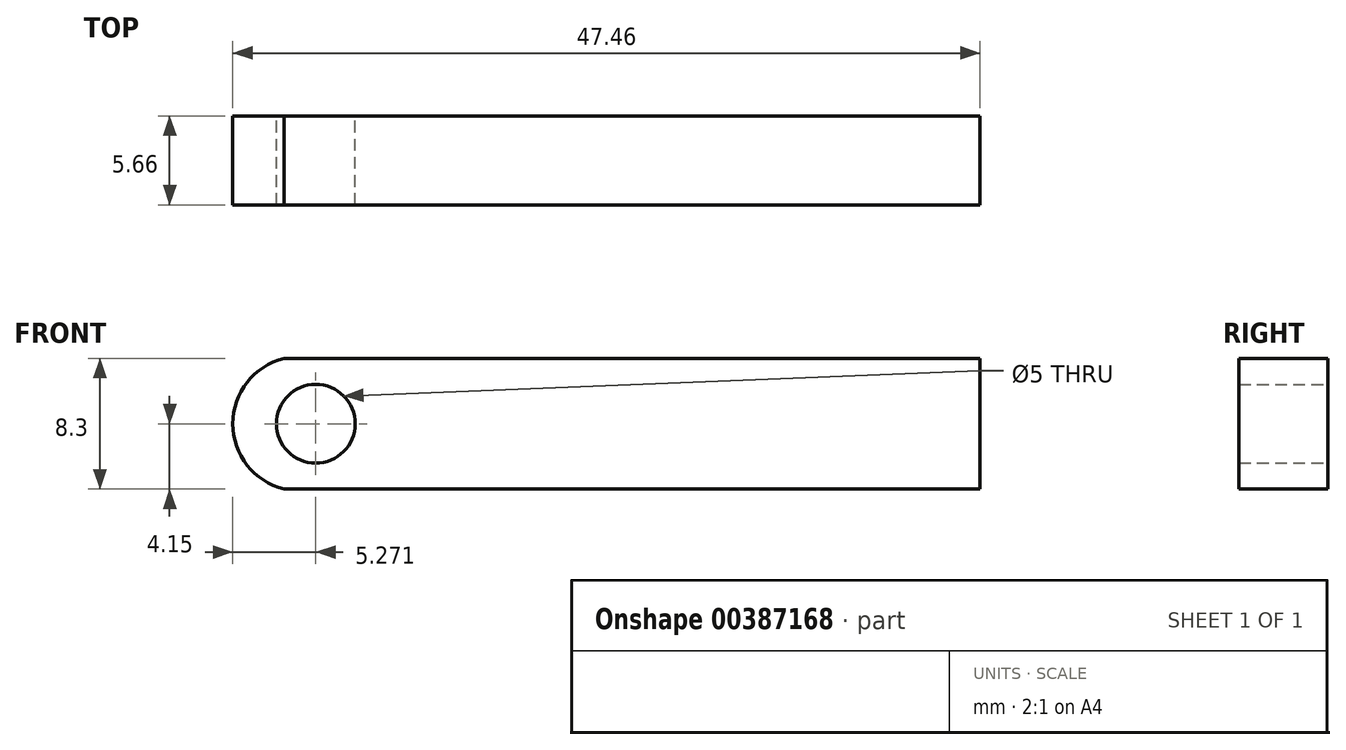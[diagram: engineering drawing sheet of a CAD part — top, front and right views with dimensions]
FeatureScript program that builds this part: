
annotation { "Feature Type Name" : "Feature", "Feature Type Description" : "" }
export const myFeature = defineFeature(function(context is Context, id is Id, definition is map)
    precondition{}
    {
        {
            var Q0;
            Q0=qCreatedBy(makeId("Front.planeOp"),FACE);
            var sketch = newSketch(context, id + "F0", { "sketchPlane" : qUnion([Q0])});
            skLineSegment(sketch, "E0", {"start": v(0, 0) * mm, "end": v(47.46, 0) * mm});
            skLineSegment(sketch, "E1", {"start": v(0, 0) * mm, "end": v(-47.46, 0) * mm});
            skLineSegment(sketch, "E2", {"start": v(0, 0) * mm, "end": v(0, 5.66) * mm});
            skLineSegment(sketch, "E3", {"start": v(0, 0) * mm, "end": v(0, -5.66) * mm});
            skLineSegment(sketch, "E4", {"start": v(47.46, 0) * mm, "end": v(44.7, 0) * mm});
            skCircle(sketch, "E5", {"center": v(42.19, 0) * mm, "radius": 2.5 * mm});
            skLineSegment(sketch, "E6", {"start": v(47.46, 0) * mm, "end": v(47.46, 4.15) * mm});
            skLineSegment(sketch, "E7", {"start": v(47.46, 4.15) * mm, "end": v(0, 4.15) * mm});
            skLineSegment(sketch, "E8.MirrorCS", {"start": v(47.46, -4.15) * mm, "end": v(0, -4.15) * mm});
            skLineSegment(sketch, "E9.MirrorCS", {"start": v(47.46, 0) * mm, "end": v(47.46, -4.15) * mm});
            skLineSegment(sketch, "E10.MirrorCS", {"start": v(-47.46, -4.15) * mm, "end": v(0, -4.15) * mm});
            skLineSegment(sketch, "E11.MirrorCS", {"start": v(-47.46, 4.15) * mm, "end": v(0, 4.15) * mm});
            skCircle(sketch, "E12.MirrorC", {"center": v(-42.19, 0) * mm, "radius": 2.5 * mm});
            skLineSegment(sketch, "E13.MirrorCS", {"start": v(-47.46, 0) * mm, "end": v(-47.46, 4.15) * mm});
            skLineSegment(sketch, "E14.MirrorCS", {"start": v(-47.46, 0) * mm, "end": v(-47.46, -4.15) * mm});
            skArc(sketch, "E15", {"start": v(-42.19, 4.15) * mm, "mid": v(-47.46, 0) * mm, "end": v(-42.19, -4.15) * mm});
            skArc(sketch, "E16.MirrorCS", {"start": v(42.19, 4.15) * mm, "mid": v(47.46, 0) * mm, "end": v(42.19, -4.15) * mm});
            skSolve(sketch);
        }
        {
            var Q0;
            {var subQ3=sQuery(id+"F0.wireOp",EDGE,"E11.MirrorCS");var subQ5=sQuery(id+"F0.wireOp",EDGE,"E15");var subQ9=makeQuery(id+"F0.imprint","INTERSECT",VERTEX,{"disambiguationData":[OD(0.0)],"derivedFrom":[subQ3,subQ5]});Q0=makeQuery(id+"F0.imprint","IMPRINT",FACE,{"disambiguationData":[TD([[makeQuery(id+"F0.imprint","IMPRINT",EDGE,{"disambiguationData":[TD([[subQ9,1.0]])],"derivedFrom":subQ3}),-1.0]])]});}
            var Q1;
            {var subQ3=sQuery(id+"F0.wireOp",EDGE,"E10.MirrorCS");var subQ5=sQuery(id+"F0.wireOp",EDGE,"E15");var subQ6=makeQuery(id+"F0.imprint","INTERSECT",VERTEX,{"disambiguationData":[OD(0.0)],"derivedFrom":[subQ3,subQ5]});Q1=makeQuery(id+"F0.imprint","IMPRINT",FACE,{"disambiguationData":[TD([[makeQuery(id+"F0.imprint","IMPRINT",EDGE,{"disambiguationData":[TD([[subQ6,1.0]])],"derivedFrom":subQ3}),1.0]])]});}
            var Q2;
            {var subQ1=sQuery(id+"F0.wireOp",EDGE,"E4");Q2=makeQuery(id+"F0.imprint","IMPRINT",FACE,{"disambiguationData":[TD([[makeQuery(id+"F0.imprint","IMPRINT",EDGE,{"derivedFrom":subQ1}),-1.0]])]});}
            var Q3;
            {var subQ1=sQuery(id+"F0.wireOp",EDGE,"E4");Q3=makeQuery(id+"F0.imprint","IMPRINT",FACE,{"disambiguationData":[TD([[makeQuery(id+"F0.imprint","IMPRINT",EDGE,{"derivedFrom":subQ1}),1.0]])]});}
            extrude(context, id + "F1", {"entities" : qUnion([Q0, Q1, Q2, Q3]), "depth" : 5.66 * mm});
        }
    });
